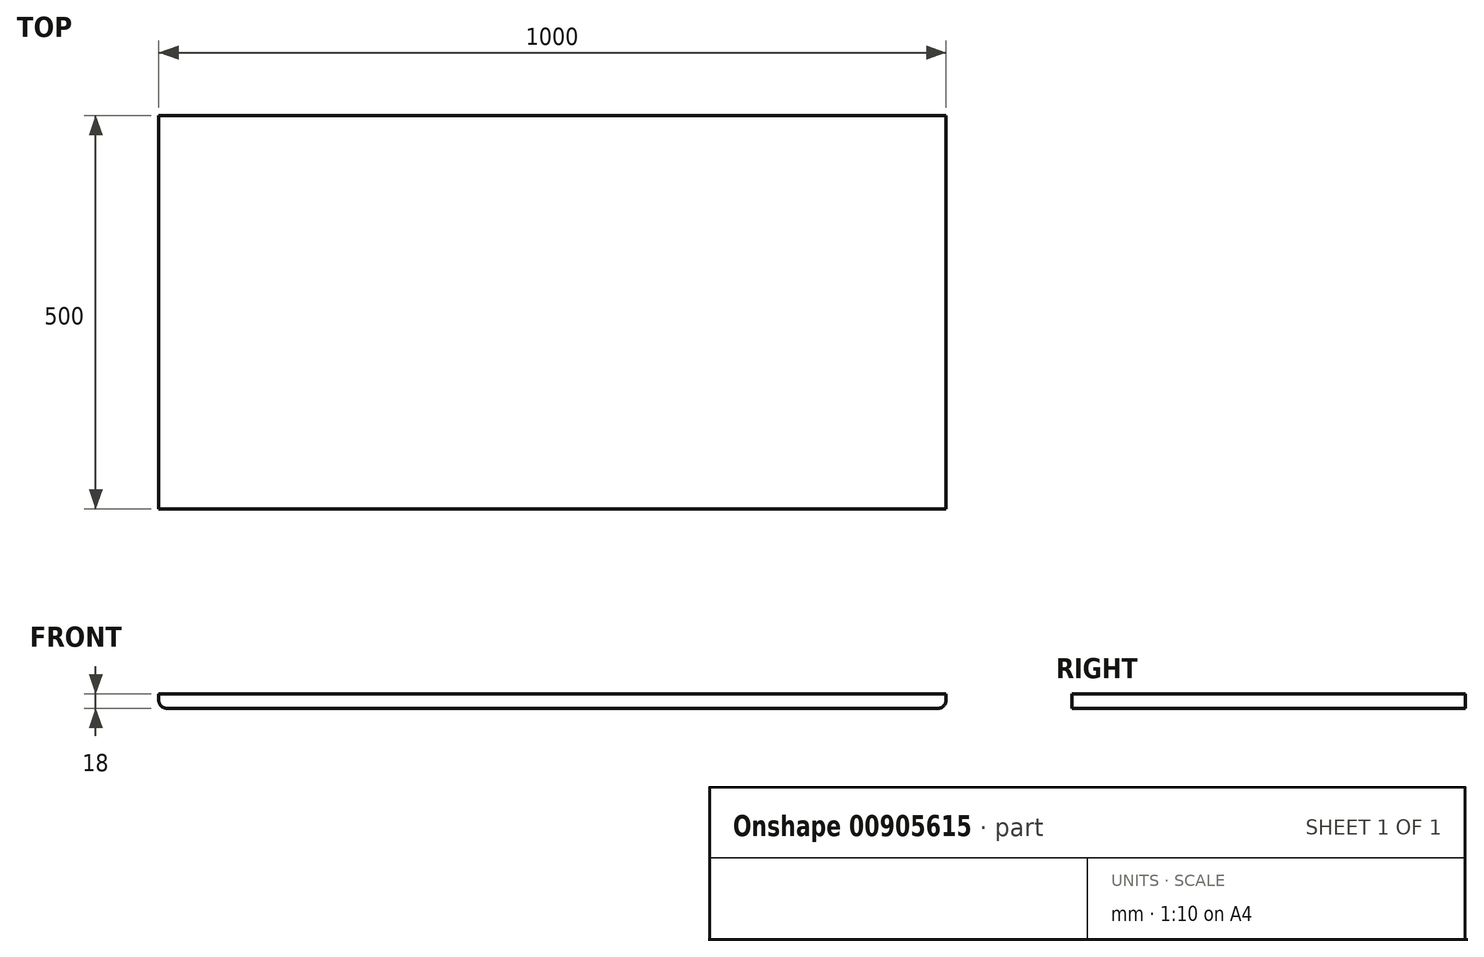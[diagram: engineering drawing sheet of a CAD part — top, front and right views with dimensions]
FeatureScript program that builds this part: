
annotation { "Feature Type Name" : "Feature", "Feature Type Description" : "" }
export const myFeature = defineFeature(function(context is Context, id is Id, definition is map)
    precondition{}
    {
        {
            var Q0;
            Q0=qCreatedBy(makeId("Top.planeOp"),FACE);
            var sketch = newSketch(context, id + "F0", { "sketchPlane" : qUnion([Q0])});
            skLineSegment(sketch, "E0.bottom", {"start": v(500, 250) * mm, "end": v(-500, 250) * mm});
            skLineSegment(sketch, "E0.top", {"start": v(500, -250) * mm, "end": v(-500, -250) * mm});
            skLineSegment(sketch, "E0.left", {"start": v(500, 250) * mm, "end": v(500, -250) * mm});
            skLineSegment(sketch, "E0.right", {"start": v(-500, 250) * mm, "end": v(-500, -250) * mm});
            skPoint(sketch, "E0.middle", {"position": v(0, 0) * mm});
            skSolve(sketch);
        }
        {
            var Q0;
            Q0=qSketchRegion(id+"F0",true);
            extrude(context, id + "F1", {"entities" : qUnion([Q0]), "depth" : 18 * mm, "offsetDistance" : 25 * mm});
        }
        {
            var Q0;
            Q0=makeQuery(id+"F1.opExtrude","CAP_EDGE",EDGE,{"disambiguationData":[OSD([sQuery(id+"F0.wireOp",EDGE,"E0.right")])],"isStart":true});
            var Q1;
            Q1=makeQuery(id+"F1.opExtrude","CAP_EDGE",EDGE,{"disambiguationData":[OSD([sQuery(id+"F0.wireOp",EDGE,"E0.left")])],"isStart":true});
            fillet(context, id + "F2", {"entities" : qUnion([Q0, Q1]), "radius" : 10 * mm, "tangentPropagation" : true, "allowEdgeOverflow" : false});
        }
    });
